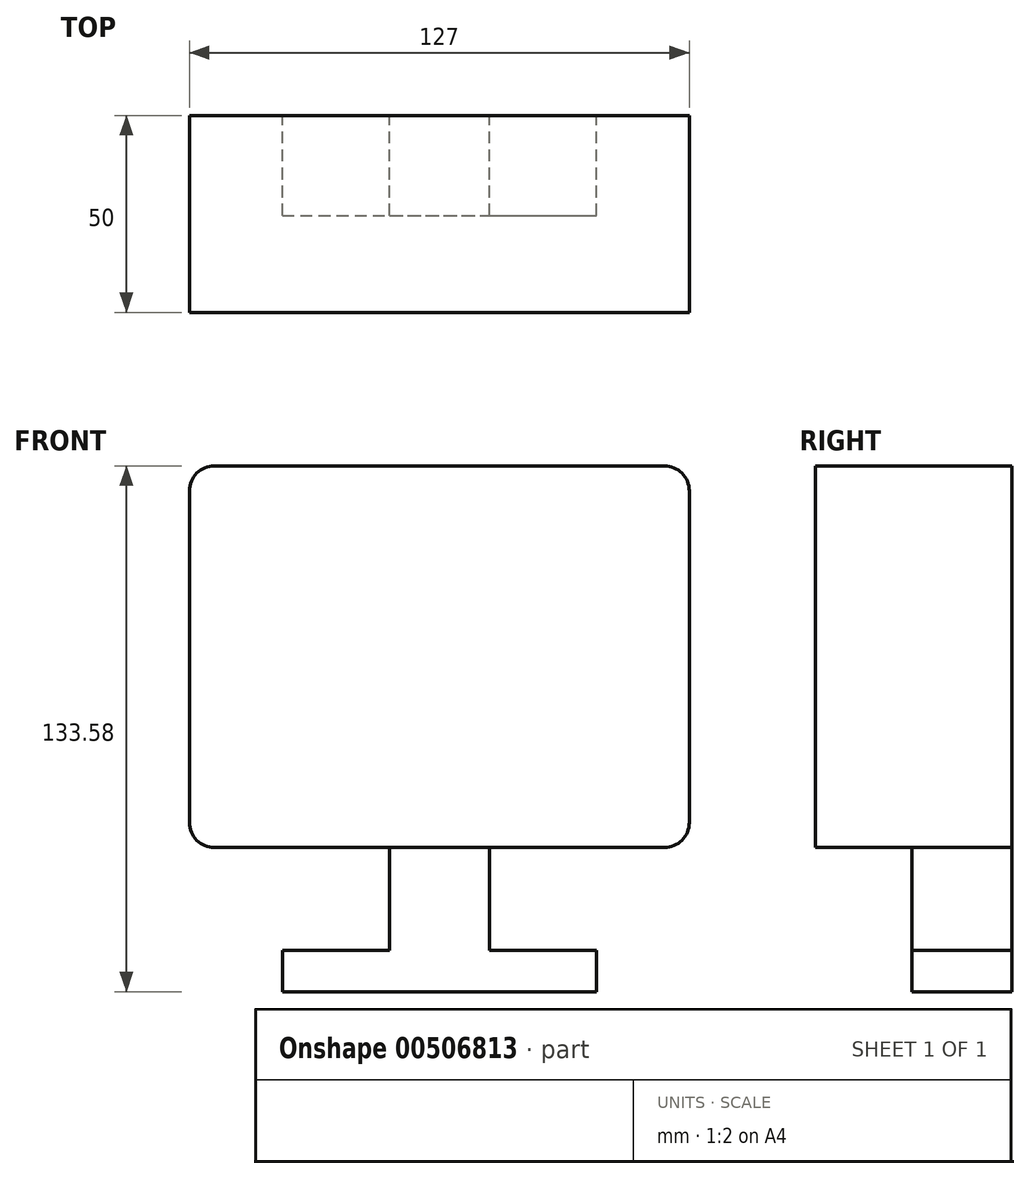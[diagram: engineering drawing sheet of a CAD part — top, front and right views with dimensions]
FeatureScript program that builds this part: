
annotation { "Feature Type Name" : "Feature", "Feature Type Description" : "" }
export const myFeature = defineFeature(function(context is Context, id is Id, definition is map)
    precondition{}
    {
        {
            var Q0;
            Q0=qCreatedBy(makeId("Front.planeOp"),FACE);
            var sketch = newSketch(context, id + "F0", { "sketchPlane" : qUnion([Q0])});
            skLineSegment(sketch, "E0.bottom", {"start": v(-71.24, 70.83) * mm, "end": v(43.06, 70.83) * mm});
            skLineSegment(sketch, "E0.top", {"start": v(-71.24, -26.14) * mm, "end": v(43.06, -26.14) * mm});
            skLineSegment(sketch, "E0.left", {"start": v(-77.59, 64.48) * mm, "end": v(-77.59, -19.8) * mm});
            skLineSegment(sketch, "E0.right", {"start": v(49.41, 64.48) * mm, "end": v(49.41, -19.8) * mm});
            skLineSegment(sketch, "E1.bottom", {"start": v(-26.79, -26.14) * mm, "end": v(-1.39, -26.14) * mm});
            skLineSegment(sketch, "E1.top", {"start": v(-26.79, -52.26) * mm, "end": v(-1.39, -52.26) * mm});
            skLineSegment(sketch, "E1.left", {"start": v(-26.79, -26.14) * mm, "end": v(-26.79, -52.26) * mm});
            skLineSegment(sketch, "E1.right", {"start": v(-1.39, -26.14) * mm, "end": v(-1.39, -52.26) * mm});
            skLineSegment(sketch, "E2.bottom", {"start": v(-53.97, -52.26) * mm, "end": v(25.79, -52.26) * mm});
            skLineSegment(sketch, "E2.top", {"start": v(-53.97, -62.75) * mm, "end": v(25.79, -62.75) * mm});
            skLineSegment(sketch, "E2.left", {"start": v(-53.97, -52.26) * mm, "end": v(-53.97, -62.75) * mm});
            skLineSegment(sketch, "E2.right", {"start": v(25.79, -52.26) * mm, "end": v(25.79, -62.75) * mm});
            skPoint(sketch, "E3.visualSharp", {"position": v(-77.59, 70.83) * mm});
            skArc(sketch, "E3.filletArc", {"start": v(-71.24, 70.83) * mm, "mid": v(-75.73, 68.97) * mm, "end": v(-77.59, 64.48) * mm});
            skPoint(sketch, "E4.visualSharp", {"position": v(-77.59, -26.14) * mm});
            skArc(sketch, "E4.filletArc", {"start": v(-77.59, -19.8) * mm, "mid": v(-75.73, -24.28) * mm, "end": v(-71.24, -26.14) * mm});
            skPoint(sketch, "E5.visualSharp", {"position": v(49.41, -26.14) * mm});
            skArc(sketch, "E5.filletArc", {"start": v(43.06, -26.14) * mm, "mid": v(47.55, -24.28) * mm, "end": v(49.41, -19.8) * mm});
            skPoint(sketch, "E6.visualSharp", {"position": v(49.41, 70.83) * mm});
            skArc(sketch, "E6.filletArc", {"start": v(49.41, 64.48) * mm, "mid": v(47.55, 68.97) * mm, "end": v(43.06, 70.83) * mm});
            skSolve(sketch);
        }
        {
            var Q0;
            Q0=makeQuery(id+"F0.imprint","IMPRINT",FACE,{"disambiguationData":[TD([[makeQuery(id+"F0.imprint","IMPRINT",EDGE,{"derivedFrom":sQuery(id+"F0.wireOp",EDGE,"E0.bottom")}),-1.0]])]});
            extrude(context, id + "F1", {"entities" : qUnion([Q0]), "depth" : 50 * mm});
        }
        {
            var Q0;
            Q0 = qSketchRegion(id + "F0", true);
            extrude(context, id + "F2", {"entities" : qUnion([Q0]), "operationType" : NewBodyOperationType.ADD, "depth" : 25.4 * mm});
        }
    });
